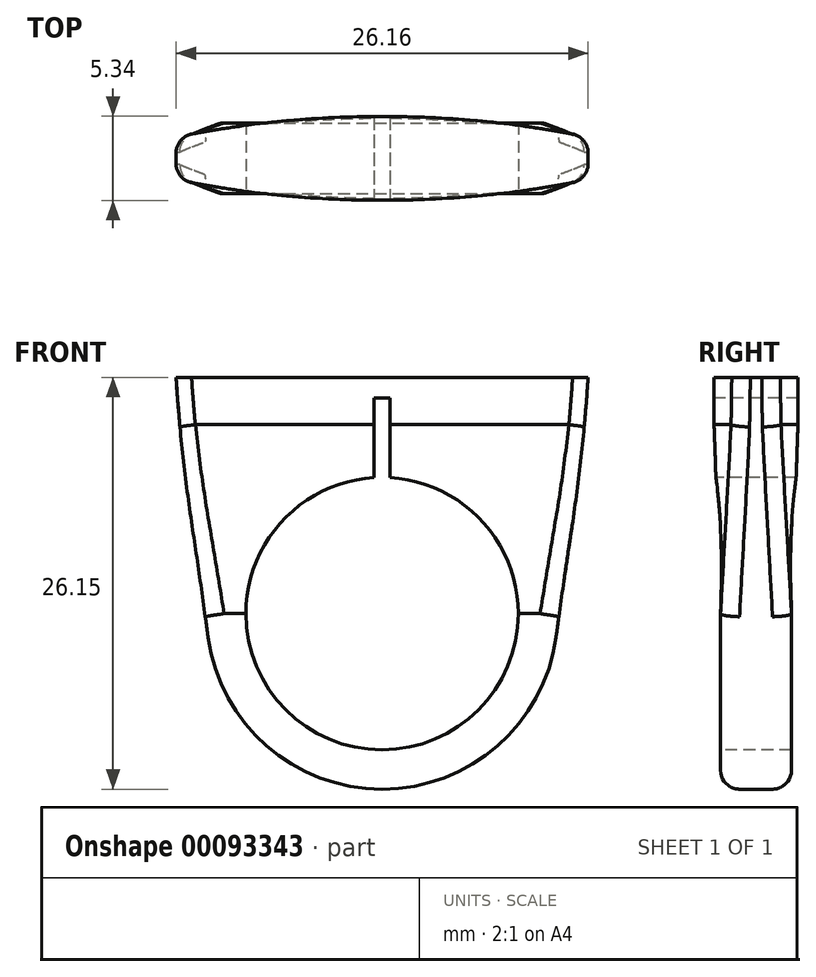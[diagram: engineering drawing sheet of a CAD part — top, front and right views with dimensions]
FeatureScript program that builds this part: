
annotation { "Feature Type Name" : "Feature", "Feature Type Description" : "" }
export const myFeature = defineFeature(function(context is Context, id is Id, definition is map)
    precondition{}
    {
        {
            var Q0;
            Q0=qCreatedBy(makeId("Front.planeOp"),FACE);
            var sketch = newSketch(context, id + "F0", { "sketchPlane" : qUnion([Q0])});
            skCircle(sketch, "E0", {"center": v(0, 0) * mm, "radius": 8.65 * mm});
            skCircle(sketch, "E1.0", {"center": v(0, 0) * mm, "radius": 11.15 * mm});
            skPoint(sketch, "E2", {"position": v(11.15, 0) * mm});
            skPoint(sketch, "E3", {"position": v(-11.15, 0) * mm});
            skLineSegment(sketch, "E4", {"start": v(11.15, 0) * mm, "end": v(11.15, 11.15) * mm});
            skLineSegment(sketch, "E5", {"start": v(11.15, 11.15) * mm, "end": v(0, 11.15) * mm});
            skLineSegment(sketch, "E6.MirrorCS", {"start": v(-11.15, 11.15) * mm, "end": v(0, 11.15) * mm});
            skLineSegment(sketch, "E7.MirrorCS", {"start": v(-11.15, 0) * mm, "end": v(-11.15, 11.15) * mm});
            skLineSegment(sketch, "E8", {"start": v(11.15, 0) * mm, "end": v(8.65, 0) * mm});
            skLineSegment(sketch, "E9", {"start": v(-11.15, 0) * mm, "end": v(-8.65, 0) * mm});
            skSolve(sketch);
        }
        {
            var Q0;
            Q0=makeQuery(id+"F0.imprint","IMPRINT",FACE,{"disambiguationData":[TD([[makeQuery(id+"F0.imprint","IMPRINT",EDGE,{"derivedFrom":sQuery(id+"F0.wireOp",EDGE,"E0")}),-1.0]])]});
            extrude(context, id + "F1", {"entities" : qUnion([Q0]), "depth" : 2.25 * mm, "hasSecondDirection" : true, "secondDirectionOppositeDirection" : true, "secondDirectionDepth" : 2.25 * mm});
        }
        {
            var Q0;
            Q0=qCreatedBy(makeId("Top.planeOp"),FACE);
            var sketch = newSketch(context, id + "F2", { "sketchPlane" : qUnion([Q0])});
            skLineSegment(sketch, "E10", {"start": v(-13.08, 0) * mm, "end": v(-13.08, -1.35) * mm});
            skLineSegment(sketch, "E11.MirrorCS", {"start": v(-13.08, 0) * mm, "end": v(-13.08, 1.35) * mm});
            skLineSegment(sketch, "E12.MirrorCS", {"start": v(13.08, 0) * mm, "end": v(13.08, 1.35) * mm});
            skLineSegment(sketch, "E13.MirrorCS", {"start": v(13.08, 0) * mm, "end": v(13.08, -1.35) * mm});
            skArc(sketch, "E14", {"start": v(13.08, 1.35) * mm, "mid": v(0, 2.67) * mm, "end": v(-13.08, 1.35) * mm});
            skArc(sketch, "E15.MirrorCS", {"start": v(13.08, -1.35) * mm, "mid": v(0, -2.67) * mm, "end": v(-13.08, -1.35) * mm});
            skLineSegment(sketch, "E16", {"start": v(0, -2.67) * mm, "end": v(0, 2.67) * mm});
            skSolve(sketch);
        }
        {
            var Q0;
            Q0=makeQuery(id+"F2.imprint","IMPRINT",FACE,{"disambiguationData":[TD([[makeQuery(id+"F2.imprint","IMPRINT",EDGE,{"derivedFrom":sQuery(id+"F2.wireOp",EDGE,"E10")}),1.0]])]});
            var Q1;
            {var subQ4=sQuery(id+"F2.wireOp",EDGE,"E12.MirrorCS");Q1=makeQuery(id+"F2.imprint","IMPRINT",FACE,{"disambiguationData":[TD([[makeQuery(id+"F2.imprint","IMPRINT",EDGE,{"derivedFrom":subQ4}),1.0]])]});}
            extrude(context, id + "F3", {"entities" : qUnion([Q0, Q1]), "depth" : 15 * mm, "hasSecondDirection" : true, "secondDirectionOppositeDirection" : false, "secondDirectionDepth" : 12 * mm});
        }
        {
            var Q0;
            Q0=qCreatedBy(makeId("Top.planeOp"),FACE);
            var sketch = newSketch(context, id + "F4", { "sketchPlane" : qUnion([Q0])});
            skPoint(sketch, "E17", {"position": v(-11.15, 2.25) * mm});
            skPoint(sketch, "E18", {"position": v(-11.15, -2.25) * mm});
            skPoint(sketch, "E19", {"position": v(11.15, 2.25) * mm});
            skPoint(sketch, "E20", {"position": v(11.15, -2.25) * mm});
            skLineSegment(sketch, "E21", {"start": v(11.15, -2.25) * mm, "end": v(11.15, 2.25) * mm});
            skLineSegment(sketch, "E22", {"start": v(-11.15, 2.25) * mm, "end": v(-11.15, -2.25) * mm});
            skLineSegment(sketch, "E23", {"start": v(-11.15, -2.25) * mm, "end": v(11.15, -2.25) * mm});
            skLineSegment(sketch, "E24", {"start": v(11.15, 2.25) * mm, "end": v(-11.15, 2.25) * mm});
            skSolve(sketch);
        }
        {
            var Q0;
            Q0=makeQuery(id+"F3.opExtrude","CAP_FACE",FACE,{"disambiguationData":[OSD([sQuery(id+"F2.wireOp",EDGE,"E10"),sQuery(id+"F2.wireOp",EDGE,"E11.MirrorCS"),sQuery(id+"F2.wireOp",EDGE,"E12.MirrorCS"),sQuery(id+"F2.wireOp",EDGE,"E13.MirrorCS"),sQuery(id+"F2.wireOp",EDGE,"E14"),sQuery(id+"F2.wireOp",EDGE,"E15.MirrorCS")])],"isStart":true});
            var Q1;
            Q1=makeQuery(id+"F4.imprint","IMPRINT",FACE,{"disambiguationData":[TD([[makeQuery(id+"F4.imprint","IMPRINT",EDGE,{"derivedFrom":sQuery(id+"F4.wireOp",EDGE,"E21")}),1.0]])]});
            loft(context, id + "F5", {"sheetProfilesArray" : [{ "sheetProfileEntities" : qUnion([Q0]) }, { "sheetProfileEntities" : qUnion([Q1]) }]});
        }
        {
            var Q0;
            {var subQ0=sQuery(id+"F0.wireOp",EDGE,"E0");var subQ1=makeQuery(id+"F0.imprint","INTERSECT",VERTEX,{"derivedFrom":[subQ0,sQuery(id+"F0.wireOp",EDGE,"E8")]});Q0=makeQuery(id+"F0.imprint","IMPRINT",FACE,{"disambiguationData":[TD([[makeQuery(id+"F0.imprint","IMPRINT",EDGE,{"disambiguationData":[TD([[subQ1,-1.0]])],"derivedFrom":subQ0}),1.0]])]});}
            extrude(context, id + "F6", {"entities" : qUnion([Q0]), "operationType" : NewBodyOperationType.REMOVE, "oppositeDirection" : true, "depth" : 3 * mm, "hasSecondDirection" : true, "secondDirectionOppositeDirection" : false, "secondDirectionDepth" : 3 * mm});
        }
        {
            var Q0;
            Q0=makeQuery(id+"F3.opExtrude","SWEPT_BODY",BODY,{"disambiguationData":[OSD([sQuery(id+"F2.wireOp",EDGE,"E10"),sQuery(id+"F2.wireOp",EDGE,"E11.MirrorCS"),sQuery(id+"F2.wireOp",EDGE,"E12.MirrorCS"),sQuery(id+"F2.wireOp",EDGE,"E13.MirrorCS"),sQuery(id+"F2.wireOp",EDGE,"E14"),sQuery(id+"F2.wireOp",EDGE,"E15.MirrorCS")])]});
            var Q1;
            Q1=makeQuery(id+"F5.opLoft","SWEPT_BODY",BODY,{"disambiguationData":[OSD([sQuery(id+"F2.wireOp",EDGE,"E10"),sQuery(id+"F2.wireOp",EDGE,"E11.MirrorCS"),sQuery(id+"F2.wireOp",EDGE,"E12.MirrorCS"),sQuery(id+"F2.wireOp",EDGE,"E13.MirrorCS"),sQuery(id+"F2.wireOp",EDGE,"E14"),sQuery(id+"F2.wireOp",EDGE,"E15.MirrorCS"),makeQuery(id+"F4.imprint","IMPRINT",FACE,{"disambiguationData":[TD([[makeQuery(id+"F4.imprint","IMPRINT",EDGE,{"derivedFrom":sQuery(id+"F4.wireOp",EDGE,"E21")}),1.0]])]})])]});
            var Q2;
            Q2=makeQuery(id+"F1.opExtrude","SWEPT_BODY",BODY,{"disambiguationData":[OSD([sQuery(id+"F0.wireOp",EDGE,"E0"),sQuery(id+"F0.wireOp",EDGE,"E1.0"),sQuery(id+"F0.wireOp",EDGE,"E8"),sQuery(id+"F0.wireOp",EDGE,"E9")])]});
            booleanBodies(context, id + "F7", {"operationType" : BooleanOperationType.UNION, "tools" : qUnion([Q0, Q1, Q2])});
        }
        {
            var Q0;
            Q0=makeQuery(id+"F7.opBoolean","MERGE",EDGE,{"derivedFrom":[makeQuery(id+"F1.opExtrude","SWEPT_EDGE",EDGE,{"disambiguationData":[OSD([sQuery(id+"F0.wireOp",EDGE,"E1.0"),sQuery(id+"F0.wireOp",EDGE,"E7.MirrorCS"),sQuery(id+"F0.wireOp",EDGE,"E9")])]}),makeQuery(id+"F5.opLoft","MID_CAP_EDGE",EDGE,{"disambiguationData":[OSD([sQuery(id+"F4.wireOp",EDGE,"E22"),sQuery(id+"F4.wireOp",EDGE,"E23"),sQuery(id+"F4.wireOp",EDGE,"E24")])],"capPos":1.0})]});
            var Q1;
            Q1=makeQuery(id+"F7.opBoolean","MERGE",EDGE,{"derivedFrom":[makeQuery(id+"F1.opExtrude","SWEPT_EDGE",EDGE,{"disambiguationData":[OSD([sQuery(id+"F0.wireOp",EDGE,"E1.0"),sQuery(id+"F0.wireOp",EDGE,"E4"),sQuery(id+"F0.wireOp",EDGE,"E8")])]}),makeQuery(id+"F5.opLoft","MID_CAP_EDGE",EDGE,{"disambiguationData":[OSD([sQuery(id+"F4.wireOp",EDGE,"E21"),sQuery(id+"F4.wireOp",EDGE,"E23"),sQuery(id+"F4.wireOp",EDGE,"E24")])],"capPos":1.0})]});
            fillet(context, id + "F8", {"entities" : qUnion([Q0, Q1]), "radius" : 467.53 * mm, "tangentPropagation" : true, "allowEdgeOverflow" : false});
        }
        {
            var Q0;
            {var subQ0=sQuery(id+"F2.wireOp",EDGE,"E11.MirrorCS");var subQ1=sQuery(id+"F2.wireOp",EDGE,"E10");Q0=makeQuery(id+"F7.opBoolean","MERGE",EDGE,{"derivedFrom":[makeQuery(id+"F3.opExtrude","CAP_EDGE",EDGE,{"disambiguationData":[OSD([subQ1,subQ0])],"isStart":true}),makeQuery(id+"F5.opLoft","MID_CAP_EDGE",EDGE,{"disambiguationData":[OSD([subQ1,subQ0,sQuery(id+"F2.wireOp",EDGE,"E14"),sQuery(id+"F2.wireOp",EDGE,"E15.MirrorCS")])],"capPos":0.0})]});}
            var Q1;
            {var subQ0=sQuery(id+"F2.wireOp",EDGE,"E13.MirrorCS");var subQ1=sQuery(id+"F2.wireOp",EDGE,"E12.MirrorCS");Q1=makeQuery(id+"F7.opBoolean","MERGE",EDGE,{"derivedFrom":[makeQuery(id+"F3.opExtrude","CAP_EDGE",EDGE,{"disambiguationData":[OSD([subQ1,subQ0])],"isStart":true}),makeQuery(id+"F5.opLoft","MID_CAP_EDGE",EDGE,{"disambiguationData":[OSD([subQ1,subQ0,sQuery(id+"F2.wireOp",EDGE,"E14"),sQuery(id+"F2.wireOp",EDGE,"E15.MirrorCS")])],"capPos":0.0})]});}
            fillet(context, id + "F9", {"entities" : qUnion([Q0, Q1]), "radius" : 109.3 * mm, "tangentPropagation" : true, "allowEdgeOverflow" : false});
        }
        {
            var Q0;
            {var subQ0=sQuery(id+"F2.wireOp",EDGE,"E15.MirrorCS");var subQ1=sQuery(id+"F2.wireOp",EDGE,"E13.MirrorCS");var subQ2=sQuery(id+"F2.wireOp",EDGE,"E12.MirrorCS");Q0=makeQuery(id+"F9.opFillet","BLEND_EDGE",EDGE,{"blendedFrom":[makeQuery(id+"F7.opBoolean","MERGE",EDGE,{"derivedFrom":[makeQuery(id+"F3.opExtrude","CAP_EDGE",EDGE,{"disambiguationData":[OSD([subQ2,subQ1])],"isStart":true}),makeQuery(id+"F5.opLoft","MID_CAP_EDGE",EDGE,{"disambiguationData":[OSD([subQ2,subQ1,sQuery(id+"F2.wireOp",EDGE,"E14"),subQ0])],"capPos":0.0})]}),makeQuery(id+"F3.opExtrude","SWEPT_FACE",FACE,{"disambiguationData":[OSD([subQ0])]})],"blendedInto":[makeQuery(id+"F3.opExtrude","SWEPT_FACE",FACE,{"disambiguationData":[OSD([subQ0])]})]});}
            var Q1;
            {var subQ0=sQuery(id+"F2.wireOp",EDGE,"E15.MirrorCS");var subQ1=sQuery(id+"F2.wireOp",EDGE,"E11.MirrorCS");var subQ2=sQuery(id+"F2.wireOp",EDGE,"E10");Q1=makeQuery(id+"F9.opFillet","BLEND_EDGE",EDGE,{"blendedFrom":[makeQuery(id+"F7.opBoolean","MERGE",EDGE,{"derivedFrom":[makeQuery(id+"F3.opExtrude","CAP_EDGE",EDGE,{"disambiguationData":[OSD([subQ2,subQ1])],"isStart":true}),makeQuery(id+"F5.opLoft","MID_CAP_EDGE",EDGE,{"disambiguationData":[OSD([subQ2,subQ1,sQuery(id+"F2.wireOp",EDGE,"E14"),subQ0])],"capPos":0.0})]}),makeQuery(id+"F3.opExtrude","SWEPT_FACE",FACE,{"disambiguationData":[OSD([subQ0])]})],"blendedInto":[makeQuery(id+"F3.opExtrude","SWEPT_FACE",FACE,{"disambiguationData":[OSD([subQ0])]})]});}
            var Q2;
            {var subQ0=sQuery(id+"F2.wireOp",EDGE,"E15.MirrorCS");var subQ1=sQuery(id+"F2.wireOp",EDGE,"E10");var subQ2=sQuery(id+"F2.wireOp",EDGE,"E11.MirrorCS");Q2=makeQuery(id+"F9.opFillet","BLEND_EDGE",EDGE,{"blendedFrom":[makeQuery(id+"F7.opBoolean","MERGE",EDGE,{"derivedFrom":[makeQuery(id+"F3.opExtrude","CAP_EDGE",EDGE,{"disambiguationData":[OSD([subQ1,subQ2])],"isStart":true}),makeQuery(id+"F5.opLoft","MID_CAP_EDGE",EDGE,{"disambiguationData":[OSD([subQ1,subQ2,sQuery(id+"F2.wireOp",EDGE,"E14"),subQ0])],"capPos":0.0})]}),makeQuery(id+"F5.opLoft","SWEPT_FACE",FACE,{"disambiguationData":[OSD([subQ1,sQuery(id+"F2.wireOp",EDGE,"E13.MirrorCS"),subQ0,sQuery(id+"F4.wireOp",EDGE,"E21"),sQuery(id+"F4.wireOp",EDGE,"E22"),sQuery(id+"F4.wireOp",EDGE,"E23")])]})],"blendedInto":[makeQuery(id+"F5.opLoft","SWEPT_FACE",FACE,{"disambiguationData":[OSD([subQ1,sQuery(id+"F2.wireOp",EDGE,"E13.MirrorCS"),subQ0,sQuery(id+"F4.wireOp",EDGE,"E21"),sQuery(id+"F4.wireOp",EDGE,"E22"),sQuery(id+"F4.wireOp",EDGE,"E23")])]})]});}
            var Q3;
            {var subQ0=sQuery(id+"F4.wireOp",EDGE,"E23");var subQ1=sQuery(id+"F4.wireOp",EDGE,"E22");Q3=makeQuery(id+"F8.opFillet","BLEND_EDGE",EDGE,{"blendedFrom":[makeQuery(id+"F7.opBoolean","MERGE",EDGE,{"derivedFrom":[makeQuery(id+"F1.opExtrude","SWEPT_EDGE",EDGE,{"disambiguationData":[OSD([sQuery(id+"F0.wireOp",EDGE,"E1.0"),sQuery(id+"F0.wireOp",EDGE,"E7.MirrorCS"),sQuery(id+"F0.wireOp",EDGE,"E9")])]}),makeQuery(id+"F5.opLoft","MID_CAP_EDGE",EDGE,{"disambiguationData":[OSD([subQ1,subQ0,sQuery(id+"F4.wireOp",EDGE,"E24")])],"capPos":1.0})]}),makeQuery(id+"F5.opLoft","SWEPT_FACE",FACE,{"disambiguationData":[OSD([sQuery(id+"F2.wireOp",EDGE,"E10"),sQuery(id+"F2.wireOp",EDGE,"E13.MirrorCS"),sQuery(id+"F2.wireOp",EDGE,"E15.MirrorCS"),sQuery(id+"F4.wireOp",EDGE,"E21"),subQ1,subQ0])]})],"blendedInto":[makeQuery(id+"F5.opLoft","SWEPT_FACE",FACE,{"disambiguationData":[OSD([sQuery(id+"F2.wireOp",EDGE,"E10"),sQuery(id+"F2.wireOp",EDGE,"E13.MirrorCS"),sQuery(id+"F2.wireOp",EDGE,"E15.MirrorCS"),sQuery(id+"F4.wireOp",EDGE,"E21"),subQ1,subQ0])]})]});}
            var Q4;
            Q4=makeQuery(id+"F1.opExtrude","CAP_EDGE",EDGE,{"disambiguationData":[OSD([sQuery(id+"F0.wireOp",EDGE,"E1.0")])],"isStart":false});
            var Q5;
            {var subQ0=sQuery(id+"F0.wireOp",EDGE,"E9");var subQ1=sQuery(id+"F0.wireOp",EDGE,"E1.0");Q5=makeQuery(id+"F8.opFillet","BLEND_EDGE",EDGE,{"blendedFrom":[makeQuery(id+"F7.opBoolean","MERGE",EDGE,{"derivedFrom":[makeQuery(id+"F1.opExtrude","SWEPT_EDGE",EDGE,{"disambiguationData":[OSD([subQ1,sQuery(id+"F0.wireOp",EDGE,"E7.MirrorCS"),subQ0])]}),makeQuery(id+"F5.opLoft","MID_CAP_EDGE",EDGE,{"disambiguationData":[OSD([sQuery(id+"F4.wireOp",EDGE,"E22"),sQuery(id+"F4.wireOp",EDGE,"E23"),sQuery(id+"F4.wireOp",EDGE,"E24")])],"capPos":1.0})]}),makeQuery(id+"F1.opExtrude","CAP_FACE",FACE,{"disambiguationData":[OSD([sQuery(id+"F0.wireOp",EDGE,"E0"),subQ1,sQuery(id+"F0.wireOp",EDGE,"E8"),subQ0])],"isStart":false})],"blendedInto":[makeQuery(id+"F1.opExtrude","CAP_FACE",FACE,{"disambiguationData":[OSD([sQuery(id+"F0.wireOp",EDGE,"E0"),subQ1,sQuery(id+"F0.wireOp",EDGE,"E8"),subQ0])],"isStart":false})]});}
            var Q6;
            {var subQ0=sQuery(id+"F0.wireOp",EDGE,"E8");var subQ1=sQuery(id+"F0.wireOp",EDGE,"E1.0");Q6=makeQuery(id+"F8.opFillet","BLEND_EDGE",EDGE,{"blendedFrom":[makeQuery(id+"F7.opBoolean","MERGE",EDGE,{"derivedFrom":[makeQuery(id+"F1.opExtrude","SWEPT_EDGE",EDGE,{"disambiguationData":[OSD([subQ1,sQuery(id+"F0.wireOp",EDGE,"E4"),subQ0])]}),makeQuery(id+"F5.opLoft","MID_CAP_EDGE",EDGE,{"disambiguationData":[OSD([sQuery(id+"F4.wireOp",EDGE,"E21"),sQuery(id+"F4.wireOp",EDGE,"E23"),sQuery(id+"F4.wireOp",EDGE,"E24")])],"capPos":1.0})]}),makeQuery(id+"F1.opExtrude","CAP_FACE",FACE,{"disambiguationData":[OSD([sQuery(id+"F0.wireOp",EDGE,"E0"),subQ1,subQ0,sQuery(id+"F0.wireOp",EDGE,"E9")])],"isStart":false})],"blendedInto":[makeQuery(id+"F1.opExtrude","CAP_FACE",FACE,{"disambiguationData":[OSD([sQuery(id+"F0.wireOp",EDGE,"E0"),subQ1,subQ0,sQuery(id+"F0.wireOp",EDGE,"E9")])],"isStart":false})]});}
            var Q7;
            {var subQ0=sQuery(id+"F4.wireOp",EDGE,"E23");var subQ1=sQuery(id+"F4.wireOp",EDGE,"E21");Q7=makeQuery(id+"F8.opFillet","BLEND_EDGE",EDGE,{"blendedFrom":[makeQuery(id+"F7.opBoolean","MERGE",EDGE,{"derivedFrom":[makeQuery(id+"F1.opExtrude","SWEPT_EDGE",EDGE,{"disambiguationData":[OSD([sQuery(id+"F0.wireOp",EDGE,"E1.0"),sQuery(id+"F0.wireOp",EDGE,"E4"),sQuery(id+"F0.wireOp",EDGE,"E8")])]}),makeQuery(id+"F5.opLoft","MID_CAP_EDGE",EDGE,{"disambiguationData":[OSD([subQ1,subQ0,sQuery(id+"F4.wireOp",EDGE,"E24")])],"capPos":1.0})]}),makeQuery(id+"F5.opLoft","SWEPT_FACE",FACE,{"disambiguationData":[OSD([sQuery(id+"F2.wireOp",EDGE,"E10"),sQuery(id+"F2.wireOp",EDGE,"E13.MirrorCS"),sQuery(id+"F2.wireOp",EDGE,"E15.MirrorCS"),subQ1,sQuery(id+"F4.wireOp",EDGE,"E22"),subQ0])]})],"blendedInto":[makeQuery(id+"F5.opLoft","SWEPT_FACE",FACE,{"disambiguationData":[OSD([sQuery(id+"F2.wireOp",EDGE,"E10"),sQuery(id+"F2.wireOp",EDGE,"E13.MirrorCS"),sQuery(id+"F2.wireOp",EDGE,"E15.MirrorCS"),subQ1,sQuery(id+"F4.wireOp",EDGE,"E22"),subQ0])]})]});}
            var Q8;
            {var subQ0=sQuery(id+"F2.wireOp",EDGE,"E15.MirrorCS");var subQ1=sQuery(id+"F2.wireOp",EDGE,"E13.MirrorCS");var subQ2=sQuery(id+"F2.wireOp",EDGE,"E12.MirrorCS");Q8=makeQuery(id+"F9.opFillet","BLEND_EDGE",EDGE,{"blendedFrom":[makeQuery(id+"F7.opBoolean","MERGE",EDGE,{"derivedFrom":[makeQuery(id+"F3.opExtrude","CAP_EDGE",EDGE,{"disambiguationData":[OSD([subQ2,subQ1])],"isStart":true}),makeQuery(id+"F5.opLoft","MID_CAP_EDGE",EDGE,{"disambiguationData":[OSD([subQ2,subQ1,sQuery(id+"F2.wireOp",EDGE,"E14"),subQ0])],"capPos":0.0})]}),makeQuery(id+"F5.opLoft","SWEPT_FACE",FACE,{"disambiguationData":[OSD([sQuery(id+"F2.wireOp",EDGE,"E10"),subQ1,subQ0,sQuery(id+"F4.wireOp",EDGE,"E21"),sQuery(id+"F4.wireOp",EDGE,"E22"),sQuery(id+"F4.wireOp",EDGE,"E23")])]})],"blendedInto":[makeQuery(id+"F5.opLoft","SWEPT_FACE",FACE,{"disambiguationData":[OSD([sQuery(id+"F2.wireOp",EDGE,"E10"),subQ1,subQ0,sQuery(id+"F4.wireOp",EDGE,"E21"),sQuery(id+"F4.wireOp",EDGE,"E22"),sQuery(id+"F4.wireOp",EDGE,"E23")])]})]});}
            var Q9;
            {var subQ0=sQuery(id+"F2.wireOp",EDGE,"E14");var subQ1=sQuery(id+"F2.wireOp",EDGE,"E13.MirrorCS");var subQ2=sQuery(id+"F2.wireOp",EDGE,"E12.MirrorCS");Q9=makeQuery(id+"F9.opFillet","BLEND_EDGE",EDGE,{"blendedFrom":[makeQuery(id+"F7.opBoolean","MERGE",EDGE,{"derivedFrom":[makeQuery(id+"F3.opExtrude","CAP_EDGE",EDGE,{"disambiguationData":[OSD([subQ2,subQ1])],"isStart":true}),makeQuery(id+"F5.opLoft","MID_CAP_EDGE",EDGE,{"disambiguationData":[OSD([subQ2,subQ1,subQ0,sQuery(id+"F2.wireOp",EDGE,"E15.MirrorCS")])],"capPos":0.0})]}),makeQuery(id+"F3.opExtrude","SWEPT_FACE",FACE,{"disambiguationData":[OSD([subQ0])]})],"blendedInto":[makeQuery(id+"F3.opExtrude","SWEPT_FACE",FACE,{"disambiguationData":[OSD([subQ0])]})]});}
            var Q10;
            {var subQ0=sQuery(id+"F2.wireOp",EDGE,"E14");var subQ1=sQuery(id+"F2.wireOp",EDGE,"E12.MirrorCS");var subQ2=sQuery(id+"F2.wireOp",EDGE,"E13.MirrorCS");Q10=makeQuery(id+"F9.opFillet","BLEND_EDGE",EDGE,{"blendedFrom":[makeQuery(id+"F7.opBoolean","MERGE",EDGE,{"derivedFrom":[makeQuery(id+"F3.opExtrude","CAP_EDGE",EDGE,{"disambiguationData":[OSD([subQ1,subQ2])],"isStart":true}),makeQuery(id+"F5.opLoft","MID_CAP_EDGE",EDGE,{"disambiguationData":[OSD([subQ1,subQ2,subQ0,sQuery(id+"F2.wireOp",EDGE,"E15.MirrorCS")])],"capPos":0.0})]}),makeQuery(id+"F5.opLoft","SWEPT_FACE",FACE,{"disambiguationData":[OSD([sQuery(id+"F2.wireOp",EDGE,"E11.MirrorCS"),subQ1,subQ0,sQuery(id+"F4.wireOp",EDGE,"E21"),sQuery(id+"F4.wireOp",EDGE,"E22"),sQuery(id+"F4.wireOp",EDGE,"E24")])]})],"blendedInto":[makeQuery(id+"F5.opLoft","SWEPT_FACE",FACE,{"disambiguationData":[OSD([sQuery(id+"F2.wireOp",EDGE,"E11.MirrorCS"),subQ1,subQ0,sQuery(id+"F4.wireOp",EDGE,"E21"),sQuery(id+"F4.wireOp",EDGE,"E22"),sQuery(id+"F4.wireOp",EDGE,"E24")])]})]});}
            var Q11;
            {var subQ0=sQuery(id+"F4.wireOp",EDGE,"E24");var subQ1=sQuery(id+"F4.wireOp",EDGE,"E21");Q11=makeQuery(id+"F8.opFillet","BLEND_EDGE",EDGE,{"blendedFrom":[makeQuery(id+"F7.opBoolean","MERGE",EDGE,{"derivedFrom":[makeQuery(id+"F1.opExtrude","SWEPT_EDGE",EDGE,{"disambiguationData":[OSD([sQuery(id+"F0.wireOp",EDGE,"E1.0"),sQuery(id+"F0.wireOp",EDGE,"E4"),sQuery(id+"F0.wireOp",EDGE,"E8")])]}),makeQuery(id+"F5.opLoft","MID_CAP_EDGE",EDGE,{"disambiguationData":[OSD([subQ1,sQuery(id+"F4.wireOp",EDGE,"E23"),subQ0])],"capPos":1.0})]}),makeQuery(id+"F5.opLoft","SWEPT_FACE",FACE,{"disambiguationData":[OSD([sQuery(id+"F2.wireOp",EDGE,"E11.MirrorCS"),sQuery(id+"F2.wireOp",EDGE,"E12.MirrorCS"),sQuery(id+"F2.wireOp",EDGE,"E14"),subQ1,sQuery(id+"F4.wireOp",EDGE,"E22"),subQ0])]})],"blendedInto":[makeQuery(id+"F5.opLoft","SWEPT_FACE",FACE,{"disambiguationData":[OSD([sQuery(id+"F2.wireOp",EDGE,"E11.MirrorCS"),sQuery(id+"F2.wireOp",EDGE,"E12.MirrorCS"),sQuery(id+"F2.wireOp",EDGE,"E14"),subQ1,sQuery(id+"F4.wireOp",EDGE,"E22"),subQ0])]})]});}
            var Q12;
            Q12=makeQuery(id+"F1.opExtrude","CAP_EDGE",EDGE,{"disambiguationData":[OSD([sQuery(id+"F0.wireOp",EDGE,"E1.0")])],"isStart":true});
            var Q13;
            {var subQ0=sQuery(id+"F0.wireOp",EDGE,"E8");var subQ1=sQuery(id+"F0.wireOp",EDGE,"E1.0");Q13=makeQuery(id+"F8.opFillet","BLEND_EDGE",EDGE,{"blendedFrom":[makeQuery(id+"F7.opBoolean","MERGE",EDGE,{"derivedFrom":[makeQuery(id+"F1.opExtrude","SWEPT_EDGE",EDGE,{"disambiguationData":[OSD([subQ1,sQuery(id+"F0.wireOp",EDGE,"E4"),subQ0])]}),makeQuery(id+"F5.opLoft","MID_CAP_EDGE",EDGE,{"disambiguationData":[OSD([sQuery(id+"F4.wireOp",EDGE,"E21"),sQuery(id+"F4.wireOp",EDGE,"E23"),sQuery(id+"F4.wireOp",EDGE,"E24")])],"capPos":1.0})]}),makeQuery(id+"F1.opExtrude","CAP_FACE",FACE,{"disambiguationData":[OSD([sQuery(id+"F0.wireOp",EDGE,"E0"),subQ1,subQ0,sQuery(id+"F0.wireOp",EDGE,"E9")])],"isStart":true})],"blendedInto":[makeQuery(id+"F1.opExtrude","CAP_FACE",FACE,{"disambiguationData":[OSD([sQuery(id+"F0.wireOp",EDGE,"E0"),subQ1,subQ0,sQuery(id+"F0.wireOp",EDGE,"E9")])],"isStart":true})]});}
            var Q14;
            {var subQ0=sQuery(id+"F0.wireOp",EDGE,"E9");var subQ1=sQuery(id+"F0.wireOp",EDGE,"E1.0");Q14=makeQuery(id+"F8.opFillet","BLEND_EDGE",EDGE,{"blendedFrom":[makeQuery(id+"F7.opBoolean","MERGE",EDGE,{"derivedFrom":[makeQuery(id+"F1.opExtrude","SWEPT_EDGE",EDGE,{"disambiguationData":[OSD([subQ1,sQuery(id+"F0.wireOp",EDGE,"E7.MirrorCS"),subQ0])]}),makeQuery(id+"F5.opLoft","MID_CAP_EDGE",EDGE,{"disambiguationData":[OSD([sQuery(id+"F4.wireOp",EDGE,"E22"),sQuery(id+"F4.wireOp",EDGE,"E23"),sQuery(id+"F4.wireOp",EDGE,"E24")])],"capPos":1.0})]}),makeQuery(id+"F1.opExtrude","CAP_FACE",FACE,{"disambiguationData":[OSD([sQuery(id+"F0.wireOp",EDGE,"E0"),subQ1,sQuery(id+"F0.wireOp",EDGE,"E8"),subQ0])],"isStart":true})],"blendedInto":[makeQuery(id+"F1.opExtrude","CAP_FACE",FACE,{"disambiguationData":[OSD([sQuery(id+"F0.wireOp",EDGE,"E0"),subQ1,sQuery(id+"F0.wireOp",EDGE,"E8"),subQ0])],"isStart":true})]});}
            var Q15;
            {var subQ0=sQuery(id+"F4.wireOp",EDGE,"E24");var subQ1=sQuery(id+"F4.wireOp",EDGE,"E22");Q15=makeQuery(id+"F8.opFillet","BLEND_EDGE",EDGE,{"blendedFrom":[makeQuery(id+"F7.opBoolean","MERGE",EDGE,{"derivedFrom":[makeQuery(id+"F1.opExtrude","SWEPT_EDGE",EDGE,{"disambiguationData":[OSD([sQuery(id+"F0.wireOp",EDGE,"E1.0"),sQuery(id+"F0.wireOp",EDGE,"E7.MirrorCS"),sQuery(id+"F0.wireOp",EDGE,"E9")])]}),makeQuery(id+"F5.opLoft","MID_CAP_EDGE",EDGE,{"disambiguationData":[OSD([subQ1,sQuery(id+"F4.wireOp",EDGE,"E23"),subQ0])],"capPos":1.0})]}),makeQuery(id+"F5.opLoft","SWEPT_FACE",FACE,{"disambiguationData":[OSD([sQuery(id+"F2.wireOp",EDGE,"E11.MirrorCS"),sQuery(id+"F2.wireOp",EDGE,"E12.MirrorCS"),sQuery(id+"F2.wireOp",EDGE,"E14"),sQuery(id+"F4.wireOp",EDGE,"E21"),subQ1,subQ0])]})],"blendedInto":[makeQuery(id+"F5.opLoft","SWEPT_FACE",FACE,{"disambiguationData":[OSD([sQuery(id+"F2.wireOp",EDGE,"E11.MirrorCS"),sQuery(id+"F2.wireOp",EDGE,"E12.MirrorCS"),sQuery(id+"F2.wireOp",EDGE,"E14"),sQuery(id+"F4.wireOp",EDGE,"E21"),subQ1,subQ0])]})]});}
            var Q16;
            {var subQ0=sQuery(id+"F2.wireOp",EDGE,"E14");var subQ1=sQuery(id+"F2.wireOp",EDGE,"E11.MirrorCS");var subQ2=sQuery(id+"F2.wireOp",EDGE,"E10");Q16=makeQuery(id+"F9.opFillet","BLEND_EDGE",EDGE,{"blendedFrom":[makeQuery(id+"F7.opBoolean","MERGE",EDGE,{"derivedFrom":[makeQuery(id+"F3.opExtrude","CAP_EDGE",EDGE,{"disambiguationData":[OSD([subQ2,subQ1])],"isStart":true}),makeQuery(id+"F5.opLoft","MID_CAP_EDGE",EDGE,{"disambiguationData":[OSD([subQ2,subQ1,subQ0,sQuery(id+"F2.wireOp",EDGE,"E15.MirrorCS")])],"capPos":0.0})]}),makeQuery(id+"F5.opLoft","SWEPT_FACE",FACE,{"disambiguationData":[OSD([subQ1,sQuery(id+"F2.wireOp",EDGE,"E12.MirrorCS"),subQ0,sQuery(id+"F4.wireOp",EDGE,"E21"),sQuery(id+"F4.wireOp",EDGE,"E22"),sQuery(id+"F4.wireOp",EDGE,"E24")])]})],"blendedInto":[makeQuery(id+"F5.opLoft","SWEPT_FACE",FACE,{"disambiguationData":[OSD([subQ1,sQuery(id+"F2.wireOp",EDGE,"E12.MirrorCS"),subQ0,sQuery(id+"F4.wireOp",EDGE,"E21"),sQuery(id+"F4.wireOp",EDGE,"E22"),sQuery(id+"F4.wireOp",EDGE,"E24")])]})]});}
            var Q17;
            {var subQ0=sQuery(id+"F2.wireOp",EDGE,"E14");var subQ1=sQuery(id+"F2.wireOp",EDGE,"E11.MirrorCS");var subQ2=sQuery(id+"F2.wireOp",EDGE,"E10");Q17=makeQuery(id+"F9.opFillet","BLEND_EDGE",EDGE,{"blendedFrom":[makeQuery(id+"F7.opBoolean","MERGE",EDGE,{"derivedFrom":[makeQuery(id+"F3.opExtrude","CAP_EDGE",EDGE,{"disambiguationData":[OSD([subQ2,subQ1])],"isStart":true}),makeQuery(id+"F5.opLoft","MID_CAP_EDGE",EDGE,{"disambiguationData":[OSD([subQ2,subQ1,subQ0,sQuery(id+"F2.wireOp",EDGE,"E15.MirrorCS")])],"capPos":0.0})]}),makeQuery(id+"F3.opExtrude","SWEPT_FACE",FACE,{"disambiguationData":[OSD([subQ0])]})],"blendedInto":[makeQuery(id+"F3.opExtrude","SWEPT_FACE",FACE,{"disambiguationData":[OSD([subQ0])]})]});}
            fillet(context, id + "F10", {"entities" : qUnion([Q0, Q1, Q2, Q3, Q4, Q5, Q6, Q7, Q8, Q9, Q10, Q11, Q12, Q13, Q14, Q15, Q16, Q17]), "radius" : 1.2 * mm, "tangentPropagation" : true, "allowEdgeOverflow" : false});
        }
        {
            var Q0;
            Q0=qCreatedBy(makeId("Front.planeOp"),FACE);
            var sketch = newSketch(context, id + "F11", { "sketchPlane" : qUnion([Q0])});
            skLineSegment(sketch, "E25.bottom", {"start": v(-0.5, 5.03) * mm, "end": v(0.5, 5.03) * mm});
            skLineSegment(sketch, "E25.top", {"start": v(-0.5, 13.71) * mm, "end": v(0.5, 13.71) * mm});
            skLineSegment(sketch, "E25.left", {"start": v(-0.5, 5.03) * mm, "end": v(-0.5, 13.71) * mm});
            skLineSegment(sketch, "E25.right", {"start": v(0.5, 5.03) * mm, "end": v(0.5, 13.71) * mm});
            skPoint(sketch, "E25.middle", {"position": v(0, 9.37) * mm});
            skSolve(sketch);
        }
        {
            var Q0;
            Q0 = qSketchRegion(id + "F11", true);
            extrude(context, id + "F12", {"entities" : qUnion([Q0]), "operationType" : NewBodyOperationType.REMOVE, "oppositeDirection" : true, "depth" : 25 * mm, "hasSecondDirection" : true, "secondDirectionOppositeDirection" : false, "secondDirectionDepth" : 25 * mm});
        }
    });
